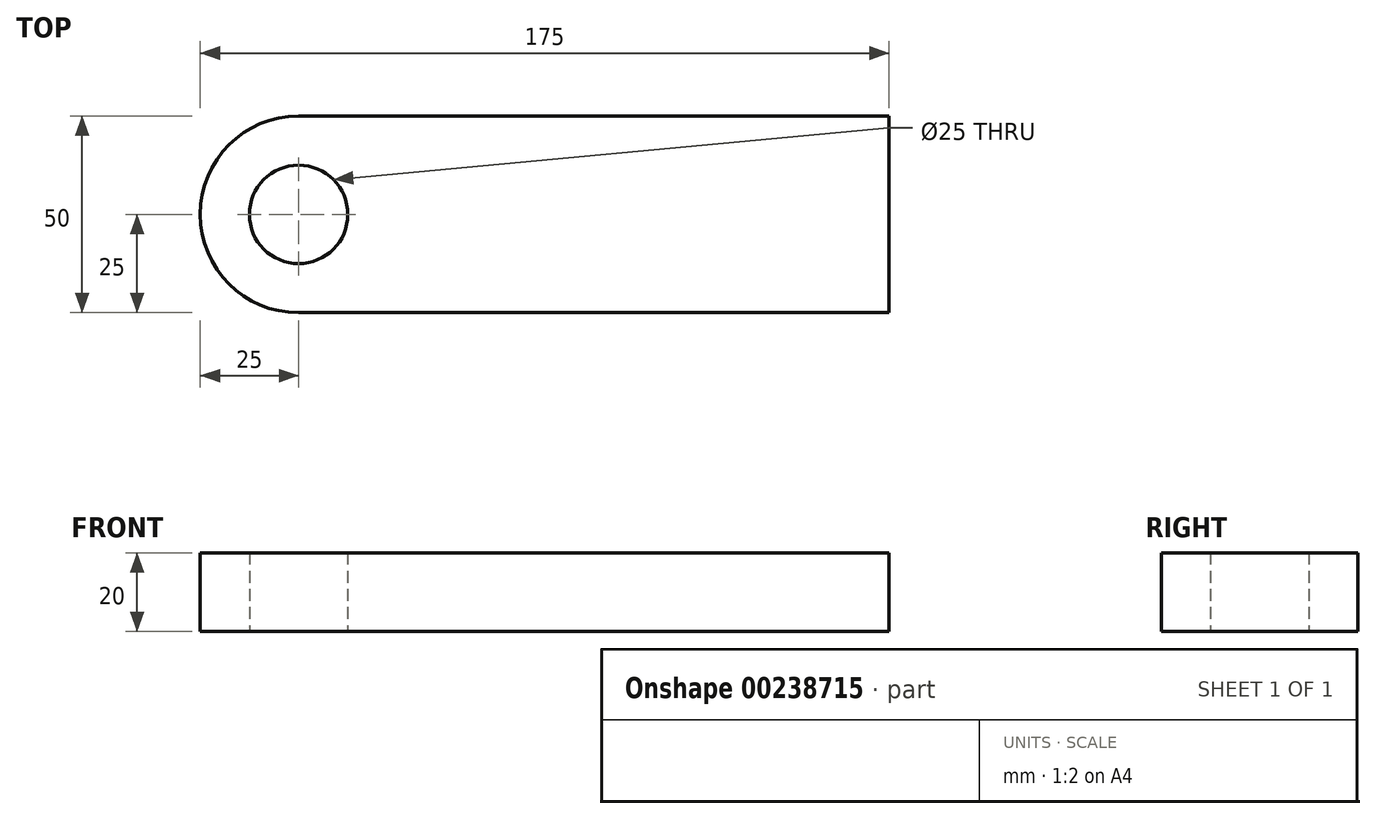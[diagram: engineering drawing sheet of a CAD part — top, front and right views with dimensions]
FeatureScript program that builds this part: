
annotation { "Feature Type Name" : "Feature", "Feature Type Description" : "" }
export const myFeature = defineFeature(function(context is Context, id is Id, definition is map)
    precondition{}
    {
        {
            var Q0;
            Q0=qCreatedBy(makeId("Top.planeOp"),FACE);
            var sketch = newSketch(context, id + "F0", { "sketchPlane" : qUnion([Q0])});
            skLineSegment(sketch, "E0.bottom", {"start": v(-75, 25) * mm, "end": v(75, 25) * mm});
            skLineSegment(sketch, "E0.top", {"start": v(-75, -25) * mm, "end": v(75, -25) * mm});
            skLineSegment(sketch, "E0.left", {"start": v(-75, 25) * mm, "end": v(-75, -25) * mm});
            skLineSegment(sketch, "E0.right", {"start": v(75, 25) * mm, "end": v(75, -25) * mm});
            skPoint(sketch, "E0.middle", {"position": v(0, 0) * mm});
            skCircle(sketch, "E1", {"center": v(-75, 0) * mm, "radius": 25 * mm});
            skCircle(sketch, "E2", {"center": v(-75, 0) * mm, "radius": 12.5 * mm});
            skSolve(sketch);
        }
        {
            var Q0;
            Q0 = qSketchRegion(id + "F0", true);
            extrude(context, id + "F1", {"entities" : qUnion([Q0]), "depth" : 20 * mm});
        }
    });
